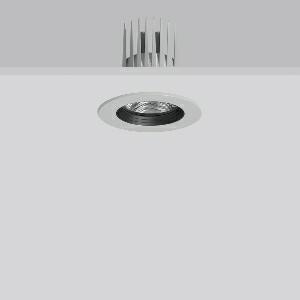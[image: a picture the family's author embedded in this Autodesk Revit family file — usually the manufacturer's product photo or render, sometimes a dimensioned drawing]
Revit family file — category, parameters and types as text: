
# Revit family: heledon_mini_e_901741_004_1_76_4ef6
name_source: partatom
category: Lighting Fixtures
units: mm (PartAtom-declared; Revit-internal decimal feet)

## family parameters
Cut with Voids When Loaded = No
Host = Face
Light Source = No
Part Type = Normal
Room Calculation Point = No
Round Connector Dimension = Use Diameter
Shared = No

## types (1)
- HELEDON mini E (1 x LED Modul 940, 2600 lm, 4000)
    Apparent Load = 20 VA
    Approval mark = CE
    CIE Flux Codes = 99 100 100 100 100
    Color Rendering = 92
    Color Temperature = 4000
    Default Elevation = 1800 mm
    Description = Series: HELEDON mini
Round recessed downlight. Housing: die-cast aluminium, powder-coated. Black plastic ring and recessed LED to prevent glare from the side. Optical assembly with reflector made of MIRO-Silver with 98% total light reflection for outstanding efficiency - can be changed without tools. Best colour rendering index Ra>90. Suitable for Recessed ceiling mounting. Installation without tools thanks to spring fastening system. Including separate LED converter with connecting cable 600 mm.High quality converter without flickering and stroboscopic effect. Through-wiring box (5 pole) available as accessory. The following accessories can be mounted without use of tools: interchangeable lenses, decorative glasses, honeycomb louvre, clear and frosted diffusers, white interchangeable plastic ring. 
Colour: silver
Diameter: 124 mm
Height: 3 mm
Cut-out diameter: 114 mm
Recess height: 170 mm
Luminaire: recess height: 120 mm
Lamp: LED
Socket: without socket
Colour temperature: 4000K
Colour rendering index (CRI): 92
System power: 20 W
Rated luminous flux: 2600 lm
Luminous efficiency: 130 lm/W
Control gear: Converter, dimmable, DALI
Protection class: II
Type of protection: IP 20
    Height = 0 mm  [stored 0 ft]
    Lamp = 1 x LED Modul 940
    Lamp Light Flux = 2600 lm
    Lamp count = 1
    Length = 124 mm  [stored 0.406824 ft]
    Lifetime = 50000 h
    Luminous efficacy = 130 lm/W
    Manufacturer = RZB
    ModVariant = No
    Model = 901741.004.1.76
    Mounting Place = Ceiling
    Mounting Type = Recessed
    Number of Poles = 1
    OnlyDefault = Yes
    Power Factor = 1
    Product Name = HELEDON mini E
    Product group = Recessed downlights
    ProductGroupID = 402
    Protection Class = Protection class II
    Protection Degree = IP 20
    RLX_Detail_Level = 1
    RLX_Emergency_Light_Flux = 0 lm
    RLX_Emergency_Type = 0
    RLX_Emergency_Type_DB = No
    RlxData = <blob elided: 125909 chars, md5=7b0f1d45>
    Socket = socket
    Standby Power = 0 W
    System Light Flux = 2600 lm
    System Power = 20 W
    Type Comments = Product without accessories
    Type Image = 901657.004.jpg
    URL = http://relux.com
    VarID = ---
    Voltage = 230 V
    Voltage Range = 220-240 V
    Weight = 0.00 kg
    Width = 0 mm  [stored 0 ft]

note: [stored X ft] marks values corroborated as IEEE doubles in the binary element streams (Revit-internal decimal feet)

## geometry (parser evidence)
native form markers: Blend x4, Sweep x9
no freeform markers — native parametric forms only
